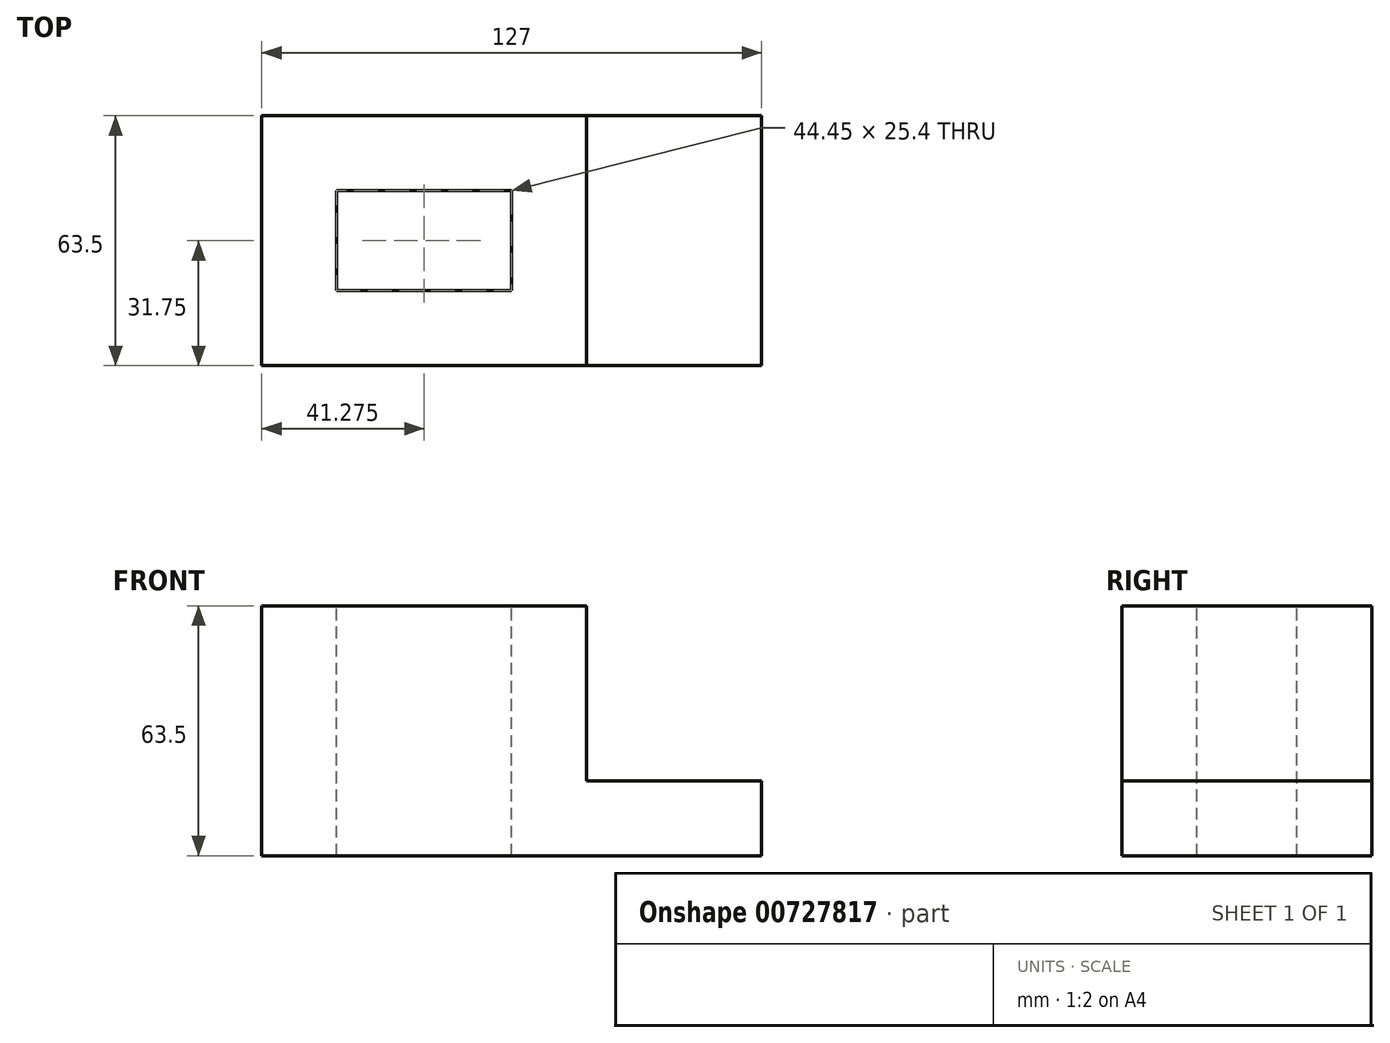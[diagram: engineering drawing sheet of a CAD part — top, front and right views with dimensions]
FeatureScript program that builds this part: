
annotation { "Feature Type Name" : "Feature", "Feature Type Description" : "" }
export const myFeature = defineFeature(function(context is Context, id is Id, definition is map)
    precondition{}
    {
        {
            var Q0;
            Q0=qCreatedBy(makeId("Top.planeOp"),FACE);
            var sketch = newSketch(context, id + "F0", { "sketchPlane" : qUnion([Q0])});
            skLineSegment(sketch, "E0", {"start": v(-82.55, 63.5) * mm, "end": v(-82.55, 0) * mm});
            skLineSegment(sketch, "E1", {"start": v(-82.55, 0) * mm, "end": v(44.45, 0) * mm});
            skLineSegment(sketch, "E2", {"start": v(44.45, 0) * mm, "end": v(44.45, 63.5) * mm});
            skLineSegment(sketch, "E3", {"start": v(44.45, 63.5) * mm, "end": v(-82.55, 63.5) * mm});
            skLineSegment(sketch, "E4", {"start": v(-63.5, 19.05) * mm, "end": v(-63.5, 44.45) * mm});
            skLineSegment(sketch, "E5", {"start": v(-63.5, 44.45) * mm, "end": v(-19.05, 44.45) * mm});
            skLineSegment(sketch, "E6", {"start": v(-19.05, 44.45) * mm, "end": v(-19.05, 0) * mm});
            skLineSegment(sketch, "E7", {"start": v(-19.05, 19.05) * mm, "end": v(-63.5, 19.05) * mm});
            skLineSegment(sketch, "E8", {"start": v(0, 63.5) * mm, "end": v(0, 0) * mm});
            skPoint(sketch, "E9", {"position": v(-63.5, 0) * mm});
            skSolve(sketch);
        }
        {
            var Q0;
            Q0 = qSketchRegion(id + "F0", true);
            extrude(context, id + "F1", {"entities" : qUnion([Q0]), "oppositeDirection" : true, "depth" : 63.5 * mm, "offsetDistance" : 25.4 * mm});
        }
        {
            var Q0;
            Q0=makeQuery(id+"F1.opExtrude","SWEPT_FACE",FACE,{"disambiguationData":[OSD([sQuery(id+"F0.wireOp",EDGE,"E1")])]});
            var sketch = newSketch(context, id + "F2", { "sketchPlane" : qUnion([Q0])});
            skLineSegment(sketch, "E10", {"start": v(0, 0) * mm, "end": v(0, -44.45) * mm});
            skLineSegment(sketch, "E11", {"start": v(0, -44.45) * mm, "end": v(44.45, -44.45) * mm});
            skSolve(sketch);
        }
        {
            var Q0;
            {var subQ0=sQuery(id+"F2.wireOp",EDGE,"E10");Q0=makeQuery(id+"F2.imprint","IMPRINT",FACE,{"disambiguationData":[TD([[makeQuery(id+"F2.imprint","IMPRINT",EDGE,{"derivedFrom":subQ0}),1.0]])]});}
            extrude(context, id + "F3", {"entities" : qUnion([Q0]), "operationType" : NewBodyOperationType.REMOVE, "endBound" : BoundingType.THROUGH_ALL, "oppositeDirection" : true, "depth" : 25.4 * mm, "offsetDistance" : 25.4 * mm});
        }
    });
